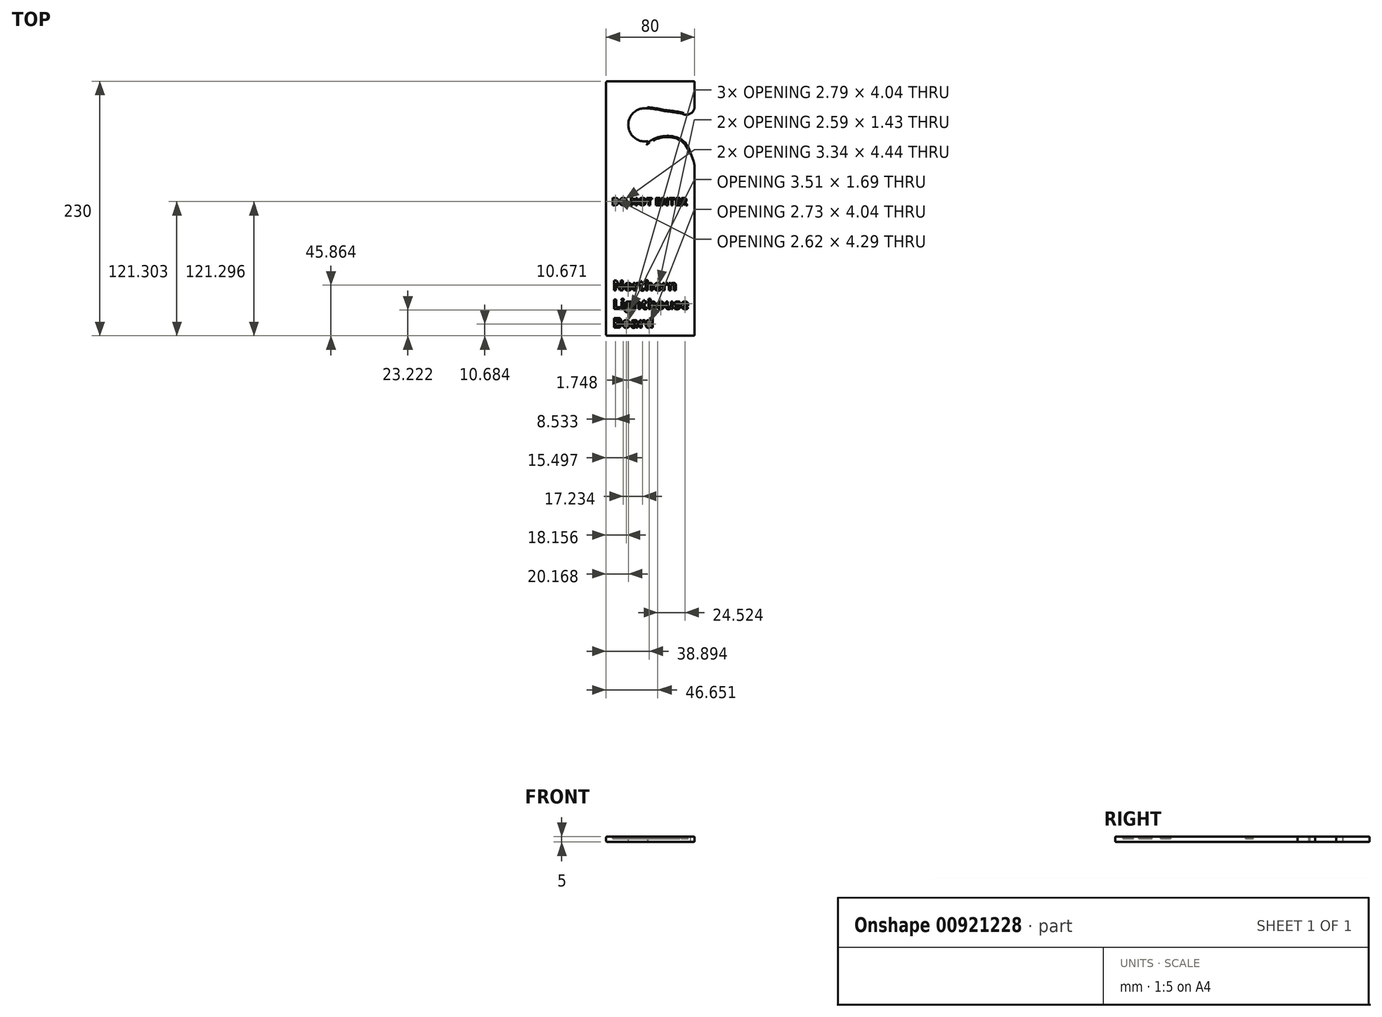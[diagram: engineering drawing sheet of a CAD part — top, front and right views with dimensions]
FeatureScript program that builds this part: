
annotation { "Feature Type Name" : "Feature", "Feature Type Description" : "" }
export const myFeature = defineFeature(function(context is Context, id is Id, definition is map)
    precondition{}
    {
        {
            var Q0;
            Q0=qCreatedBy(makeId("Top.planeOp"),FACE);
            var sketch = newSketch(context, id + "F0", { "sketchPlane" : qUnion([Q0])});
            skLineSegment(sketch, "E0.bottom", {"start": v(-38.66, 92.21) * mm, "end": v(41.34, 92.21) * mm});
            skLineSegment(sketch, "E0.top", {"start": v(-38.66, -137.79) * mm, "end": v(41.34, -137.79) * mm});
            skLineSegment(sketch, "E0.left", {"start": v(-38.66, 92.21) * mm, "end": v(-38.66, -137.79) * mm});
            skLineSegment(sketch, "E0.right", {"start": v(41.34, 92.21) * mm, "end": v(41.34, -137.79) * mm});
            skCircle(sketch, "E1", {"center": v(-3.66, 52.86) * mm, "radius": 15 * mm});
            skFitSpline(sketch, "E2", {"points": [v(-1.25, 67.67) * mm, v(16.56, 65.01) * mm, v(41.34, 53.88) * mm, v(41.34, 17.2) * mm, v(32.93, 36.37) * mm, v(-1.02, 36.86) * mm], "startDerivative": vector(99.25, 0.2) * mm, "endDerivative": vector(-134.25, -103.4) * mm});
            skLineSegment(sketch, "E3", {"start": v(-1.25, 67.67) * mm, "end": v(-1.25, 67.67) * mm});
            skLineSegment(sketch, "E4", {"start": v(0, 37.6) * mm, "end": v(-1.02, 36.86) * mm});
            skLineSegment(sketch, "E5", {"start": v(-1.02, 36.86) * mm, "end": v(-1.25, 67.67) * mm});
            skSolve(sketch);
        }
        {
            var Q0;
            {var subQ1=sQuery(id+"F0.wireOp",EDGE,"E0.bottom");Q0=makeQuery(id+"F0.imprint","IMPRINT",FACE,{"disambiguationData":[TD([[makeQuery(id+"F0.imprint","IMPRINT",EDGE,{"derivedFrom":subQ1}),-1.0]])]});}
            extrude(context, id + "F1", {"entities" : qUnion([Q0]), "depth" : 5 * mm, "offsetDistance" : 25 * mm});
        }
        {
            var Q0;
            Q0=makeQuery(id+"F1.opExtrude","CAP_FACE",FACE,{"disambiguationData":[OSD([sQuery(id+"F0.wireOp",EDGE,"E0.bottom"),sQuery(id+"F0.wireOp",EDGE,"E0.top"),sQuery(id+"F0.wireOp",EDGE,"E0.left"),sQuery(id+"F0.wireOp",EDGE,"E0.right"),sQuery(id+"F0.wireOp",EDGE,"E1"),sQuery(id+"F0.wireOp",EDGE,"E2"),sQuery(id+"F0.wireOp",EDGE,"E3"),sQuery(id+"F0.wireOp",EDGE,"E4"),sQuery(id+"F0.wireOp",EDGE,"E5")])],"isStart":false});
            var sketch = newSketch(context, id + "F2", { "sketchPlane" : qUnion([Q0])});
            skSolve(sketch);
        }
        {
            var Q0;
            {var subQ5=sQuery(id+"F0.wireOp",EDGE,"E4");Q0=makeQuery(id+"F0.imprint","IMPRINT",FACE,{"disambiguationData":[TD([[makeQuery(id+"F0.imprint","IMPRINT",EDGE,{"derivedFrom":subQ5}),-1.0]])]});}
            extrude(context, id + "F3", {"entities" : qUnion([Q0]), "operationType" : NewBodyOperationType.ADD, "depth" : 5 * mm, "offsetDistance" : 25 * mm});
        }
        {
            var Q0;
            {var subQ1=sQuery(id+"F0.wireOp",EDGE,"E0.bottom");Q0=makeQuery(id+"F2.imprint","IMPRINT",FACE,{"disambiguationData":[TD([[makeQuery(id+"F2.imprint","IMPRINT",EDGE,{"derivedFrom":makeQuery(id+"F1.opExtrude","CAP_EDGE",EDGE,{"disambiguationData":[OSD([subQ1])],"isStart":false})}),-1.0]])]});}
            var sketch = newSketch(context, id + "F4", { "sketchPlane" : qUnion([Q0])});
            skSolve(sketch);
        }
        {
            var Q0;
            {var subQ1=sQuery(id+"F0.wireOp",EDGE,"E0.bottom");Q0=makeQuery(id+"F4.imprint","IMPRINT",FACE,{"disambiguationData":[TD([[makeQuery(id+"F4.imprint","IMPRINT",EDGE,{"derivedFrom":makeQuery(id+"F2.imprint","IMPRINT",EDGE,{"derivedFrom":makeQuery(id+"F1.opExtrude","CAP_EDGE",EDGE,{"disambiguationData":[OSD([subQ1])],"isStart":false})})}),-1.0]])]});}
            var sketch = newSketch(context, id + "F5", { "sketchPlane" : qUnion([Q0])});
            skCircle(sketch, "E6", {"center": v(33.7, 69.64) * mm, "radius": 7.64 * mm});
            skLineSegment(sketch, "E7", {"start": v(37.82, 27.1) * mm, "end": v(41.34, 17.2) * mm});
            skLineSegment(sketch, "E8", {"start": v(41.34, 17.2) * mm, "end": v(40.84, 16.05) * mm});
            skLineSegment(sketch, "E9", {"start": v(40.84, 16.05) * mm, "end": v(37.82, 27.1) * mm});
            skSolve(sketch);
        }
        {
            var Q0;
            Q0 = qSketchRegion(id + "F5", true);
            extrude(context, id + "F6", {"entities" : qUnion([Q0]), "operationType" : NewBodyOperationType.ADD, "oppositeDirection" : true, "depth" : 5 * mm, "offsetDistance" : 25 * mm});
        }
        {
            var Q0;
            {var subQ0=sQuery(id+"F5.wireOp",EDGE,"E6");var subQ1=sQuery(id+"F0.wireOp",EDGE,"E0.right");var subQ4=makeQuery(id+"F4.imprint","IMPRINT",EDGE,{"derivedFrom":makeQuery(id+"F2.imprint","IMPRINT",EDGE,{"derivedFrom":makeQuery(id+"F1.opExtrude","CAP_EDGE",EDGE,{"disambiguationData":[OSD([subQ1]),TDD([makeQuery(id+"F0.imprint","IMPRINT",EDGE,{"disambiguationData":[TD([[makeQuery(id+"F0.imprint","INTERSECT",VERTEX,{"derivedFrom":[sQuery(id+"F0.wireOp",EDGE,"E0.bottom"),subQ1]}),-1.0]])],"derivedFrom":subQ1})])],"isStart":false})})});var subQ5=makeQuery(id+"F5.imprint","INTERSECT",VERTEX,{"derivedFrom":[subQ4,subQ0]});Q0=makeQuery(id+"F5.imprint","IMPRINT",FACE,{"disambiguationData":[TD([[makeQuery(id+"F5.imprint","IMPRINT",EDGE,{"disambiguationData":[TD([[subQ5,1.0]])],"derivedFrom":subQ0}),-1.0]])]});}
            extrude(context, id + "F7", {"entities" : qUnion([Q0]), "operationType" : NewBodyOperationType.REMOVE, "oppositeDirection" : true, "depth" : 25 * mm, "offsetDistance" : 25 * mm});
        }
        {
            var Q0;
            {var subQ0=sQuery(id+"F0.wireOp",EDGE,"E2");var subQ1=sQuery(id+"F0.wireOp",EDGE,"E0.right");Q0=makeQuery(id+"F6.boolean.opBoolean","MERGE",EDGE,{"derivedFrom":[makeQuery(id+"F1.opExtrude","SWEPT_EDGE",EDGE,{"disambiguationData":[OSD([subQ1,subQ0]),TDD([makeQuery(id+"F0.imprint","INTERSECT",VERTEX,{"disambiguationData":[OD(1.0)],"derivedFrom":[subQ1,subQ0]})])]}),makeQuery(id+"F6.opExtrude","SWEPT_EDGE",EDGE,{"disambiguationData":[OSD([subQ1,subQ0,sQuery(id+"F5.wireOp",EDGE,"E7"),sQuery(id+"F5.wireOp",EDGE,"E8")])]})]});}
            fillet(context, id + "F8", {"entities" : qUnion([Q0]), "radius" : 20 * mm, "tangentPropagation" : true, "allowEdgeOverflow" : false});
        }
        {
            var Q0;
            {var subQ0=sQuery(id+"F0.wireOp",EDGE,"E5");var subQ1=sQuery(id+"F0.wireOp",EDGE,"E4");var subQ2=sQuery(id+"F0.wireOp",EDGE,"E2");var subQ3=sQuery(id+"F0.wireOp",EDGE,"E1");Q0=makeQuery(id+"F6.boolean.opBoolean","MERGE",FACE,{"derivedFrom":[makeQuery(id+"F3.boolean.opBoolean","MERGE",FACE,{"derivedFrom":[makeQuery(id+"F1.opExtrude","CAP_FACE",FACE,{"disambiguationData":[OSD([sQuery(id+"F0.wireOp",EDGE,"E0.bottom"),sQuery(id+"F0.wireOp",EDGE,"E0.top"),sQuery(id+"F0.wireOp",EDGE,"E0.left"),sQuery(id+"F0.wireOp",EDGE,"E0.right"),subQ3,subQ2,subQ1,subQ0])],"isStart":false}),makeQuery(id+"F3.opExtrude","CAP_FACE",FACE,{"disambiguationData":[OSD([subQ3,subQ2,subQ1,subQ0])],"isStart":false})]}),makeQuery(id+"F6.opExtrude","CAP_FACE",FACE,{"disambiguationData":[OSD([sQuery(id+"F5.wireOp",EDGE,"E7"),sQuery(id+"F5.wireOp",EDGE,"E8"),sQuery(id+"F5.wireOp",EDGE,"E9")])],"isStart":true})]});}
            var Q1;
            {var subQ0=sQuery(id+"F0.wireOp",EDGE,"E5");var subQ1=sQuery(id+"F0.wireOp",EDGE,"E4");var subQ2=sQuery(id+"F0.wireOp",EDGE,"E2");var subQ3=sQuery(id+"F0.wireOp",EDGE,"E1");Q1=makeQuery(id+"F6.boolean.opBoolean","MERGE",FACE,{"derivedFrom":[makeQuery(id+"F3.boolean.opBoolean","MERGE",FACE,{"derivedFrom":[makeQuery(id+"F1.opExtrude","CAP_FACE",FACE,{"disambiguationData":[OSD([sQuery(id+"F0.wireOp",EDGE,"E0.bottom"),sQuery(id+"F0.wireOp",EDGE,"E0.top"),sQuery(id+"F0.wireOp",EDGE,"E0.left"),sQuery(id+"F0.wireOp",EDGE,"E0.right"),subQ3,subQ2,subQ1,subQ0])],"isStart":true}),makeQuery(id+"F3.opExtrude","CAP_FACE",FACE,{"disambiguationData":[OSD([subQ3,subQ2,subQ1,subQ0])],"isStart":true})]}),makeQuery(id+"F6.opExtrude","CAP_FACE",FACE,{"disambiguationData":[OSD([sQuery(id+"F5.wireOp",EDGE,"E7"),sQuery(id+"F5.wireOp",EDGE,"E8"),sQuery(id+"F5.wireOp",EDGE,"E9")])],"isStart":false})]});}
            var Q2;
            Q2=makeQuery(id+"F1.opExtrude","SWEPT_EDGE",EDGE,{"disambiguationData":[OSD([sQuery(id+"F0.wireOp",EDGE,"E0.bottom"),sQuery(id+"F0.wireOp",EDGE,"E0.right")])]});
            var Q3;
            Q3=makeQuery(id+"F1.opExtrude","SWEPT_EDGE",EDGE,{"disambiguationData":[OSD([sQuery(id+"F0.wireOp",EDGE,"E0.bottom"),sQuery(id+"F0.wireOp",EDGE,"E0.left")])]});
            var Q4;
            Q4=makeQuery(id+"F1.opExtrude","SWEPT_EDGE",EDGE,{"disambiguationData":[OSD([sQuery(id+"F0.wireOp",EDGE,"E0.top"),sQuery(id+"F0.wireOp",EDGE,"E0.right")])]});
            var Q5;
            Q5=makeQuery(id+"F1.opExtrude","SWEPT_EDGE",EDGE,{"disambiguationData":[OSD([sQuery(id+"F0.wireOp",EDGE,"E0.top"),sQuery(id+"F0.wireOp",EDGE,"E0.left")])]});
            fillet(context, id + "F9", {"entities" : qUnion([Q0, Q1, Q2, Q3, Q4, Q5]), "radius" : 1 * mm, "tangentPropagation" : true, "allowEdgeOverflow" : false});
        }
        {
            var Q0;
            Q0=makeQuery(id+"F5.imprint","IMPRINT",FACE,{"disambiguationData":[TD([[makeQuery(id+"F5.imprint","IMPRINT",EDGE,{"derivedFrom":sQuery(id+"F5.wireOp",EDGE,"E8")}),1.0]])]});
            var sketch = newSketch(context, id + "F10", { "sketchPlane" : qUnion([Q0])});
            skText(sketch, "E10", { "text": "Northern \nLighthouse \nBoard", "fontName": "OpenSans-Bold.ttf"});
            const initialGuessF10  = {"E10": [-0.03266, -0.09679, 1, 0, 0.00892]};
            skSetInitialGuess(sketch, initialGuessF10);
            skSolve(sketch);
        }
        {
            var Q0;
            Q0 = qSketchRegion(id + "F10", true);
            extrude(context, id + "F11", {"entities" : qUnion([Q0]), "oppositeDirection" : true, "depth" : 2 * mm, "offsetDistance" : 25 * mm});
        }
        {
            var Q0;
            {var subQ1=sQuery(id+"F0.wireOp",EDGE,"E0.bottom");Q0=makeQuery(id+"F2.imprint","IMPRINT",FACE,{"disambiguationData":[TD([[makeQuery(id+"F2.imprint","IMPRINT",EDGE,{"derivedFrom":makeQuery(id+"F1.opExtrude","CAP_EDGE",EDGE,{"disambiguationData":[OSD([subQ1])],"isStart":false})}),-1.0]])]});}
            var sketch = newSketch(context, id + "F12", { "sketchPlane" : qUnion([Q0])});
            skText(sketch, "E11", { "text": "DO NOT ENTER", "fontName": "OpenSans-Bold.ttf"});
            const initialGuessF12  = {"E11": [-0.03366, -0.01979, 1, 0, 0.00664]};
            skSetInitialGuess(sketch, initialGuessF12);
            skSolve(sketch);
        }
        {
            var Q0;
            Q0 = qSketchRegion(id + "F12", true);
            extrude(context, id + "F13", {"entities" : qUnion([Q0]), "oppositeDirection" : true, "depth" : 2 * mm, "offsetDistance" : 25 * mm});
        }
    });
